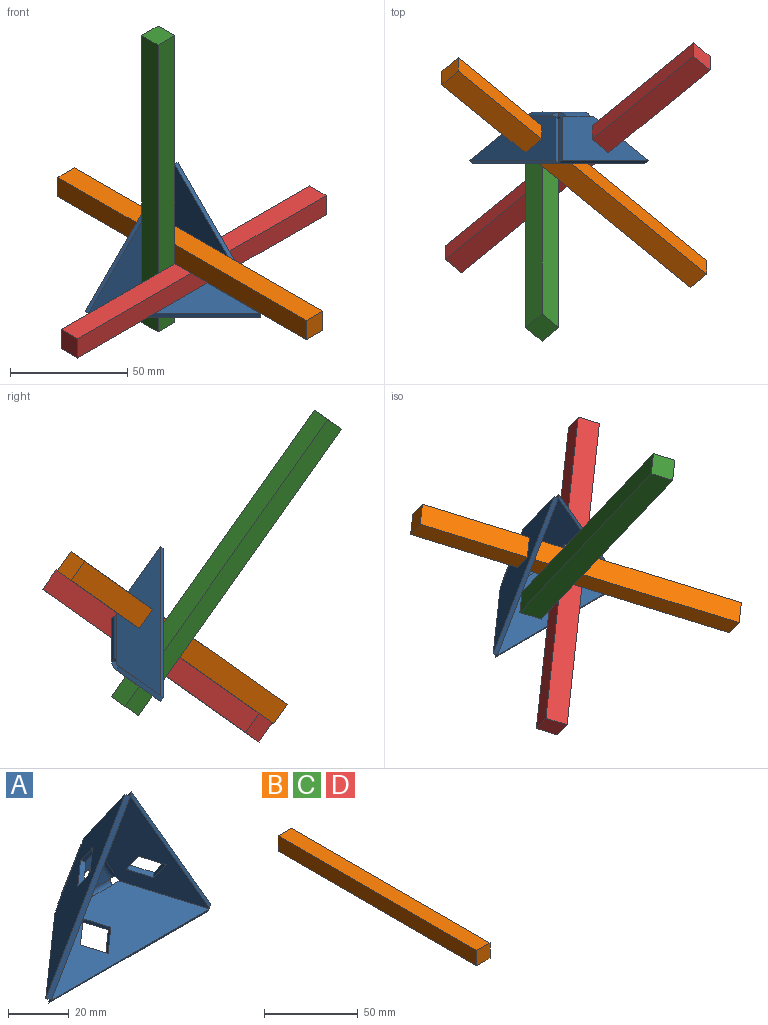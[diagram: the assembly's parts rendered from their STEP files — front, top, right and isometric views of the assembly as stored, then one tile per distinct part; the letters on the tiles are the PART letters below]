
ASSEMBLY  parts=4 mates=6
PART A: 48 faces, bbox 76.5x21.9x66.3 mm
  f0: cylinder r=2.75mm len=5.5mm, axis (0,-1,0), area 34.6mm2, adj f1,f2
  f1: plane 20.9x18.1mm, normal (0,1,0), area 165.4mm2, adj f0,f16,f31,f46
  f2: plane 20.9x18.1mm, normal (0,-1,0), area 165.4mm2, adj f0,f17,f32,f47
  f3: plane 3.59x3.01mm, normal (0.5,0.82,-0.29), area 6.4mm2, adj f5,f12,f13,f14
  f4: plane 64.61x38.24mm, normal (-0.5,-0.82,0.29), area 147.3mm2, adj f5,f11,f12,f13
  f5: plane 27.58x20.08mm, normal (0.71,0.58,0.41), area 65.6mm2, adj f3,f4,f12,f13
  f6: plane 3.59x3.01mm, normal (0.5,0.82,-0.29), area 6.4mm2, adj f11,f12,f13,f15
  f7: plane 8.49x6.93mm, normal (0,0.58,-0.82), area 20mm2, adj f8,f10,f12,f13
  f8: plane 8.98x6.93mm, normal (0.71,0.58,0.41), area 20mm2, adj f7,f9,f12,f13
  f9: plane 8.49x6.93mm, normal (0,-0.58,0.82), area 20mm2, adj f8,f10,f12,f13
  f10: plane 8.98x6.93mm, normal (-0.71,-0.58,-0.41), area 20mm2, adj f7,f9,f12,f13
  f11: plane 24.6x20.08mm, normal (0,0.58,-0.82), area 65.6mm2, adj f4,f6,f12,f13
  f12: plane 63.79x36.83mm, normal (-0.71,0.58,0.41), area 1070.1mm2, adj f3,f4,f5,f6,f7,f8,f9,f10
  f13: plane 63.79x36.83mm, normal (0.71,-0.58,-0.41), area 1070.1mm2, adj f3,f4,f5,f6,f7,f8,f9,f10
  f14: plane 3.03x2.97mm, normal (0.5,0,0.87), area 6.3mm2, adj f3,f16,f17,f30
  f15: plane 3.03x2.97mm, normal (-0.5,0,-0.87), area 6.3mm2, adj f6,f16,f17,f44
  f16: cylinder r=4.29mm len=19.85mm, axis (0.5,0,0.87), area 85.6mm2, adj f1,f12,f14,f15
  f17: cylinder r=2.29mm len=19.03mm, axis (0.5,0,0.87), area 45.6mm2, adj f2,f13,f14,f15
  f18: plane 3.59x3.01mm, normal (-0.5,0.82,-0.29), area 6.4mm2, adj f20,f27,f28,f29
  f19: plane 64.61x38.24mm, normal (0.5,-0.82,0.29), area 147.3mm2, adj f20,f26,f27,f28
  f20: plane 24.6x20.08mm, normal (0,0.58,-0.82), area 65.6mm2, adj f18,f19,f27,f28
  f21: plane 3.59x3.01mm, normal (-0.5,0.82,-0.29), area 6.4mm2, adj f26,f27,f28,f30
  f22: plane 8.98x6.93mm, normal (-0.71,0.58,0.41), area 20mm2, adj f23,f25,f27,f28
  f23: plane 8.49x6.93mm, normal (0,0.58,-0.82), area 20mm2, adj f22,f24,f27,f28
  f24: plane 8.98x6.93mm, normal (0.71,-0.58,-0.41), area 20mm2, adj f23,f25,f27,f28
  f25: plane 8.49x6.93mm, normal (0,-0.58,0.82), area 20mm2, adj f22,f24,f27,f28
  f26: plane 27.58x20.08mm, normal (-0.71,0.58,0.41), area 65.6mm2, adj f19,f21,f27,f28
  f27: plane 63.79x36.83mm, normal (0.71,0.58,0.41), area 1070.1mm2, adj f18,f19,f20,f21,f22,f23,f24,f25
  f28: plane 63.79x36.83mm, normal (-0.71,-0.58,-0.41), area 1070.1mm2, adj f18,f19,f20,f21,f22,f23,f24,f25
  f29: plane 3.03x2.97mm, normal (0.5,0,-0.87), area 6.3mm2, adj f18,f31,f32,f45
  f30: plane 3.03x2.97mm, normal (-0.5,0,0.87), area 6.3mm2, adj f14,f21,f31,f32
  f31: cylinder r=4.29mm len=19.85mm, axis (0.5,0,-0.87), area 85.6mm2, adj f1,f27,f29,f30
  f32: cylinder r=2.29mm len=19.03mm, axis (0.5,0,-0.87), area 45.6mm2, adj f2,f28,f29,f30
  f33: plane 3.2x1.63mm, normal (0,0.82,0.58), area 6.4mm2, adj f35,f42,f43,f44
  f34: plane 73.66x1.63mm, normal (0,-0.82,-0.58), area 147.3mm2, adj f35,f41,f42,f43
  f35: plane 23.18x20.08mm, normal (-0.71,0.58,0.41), area 65.6mm2, adj f33,f34,f42,f43
  f36: plane 3.2x1.63mm, normal (0,0.82,0.58), area 6.4mm2, adj f41,f42,f43,f45
  f37: plane 7.07x6.93mm, normal (0.71,0.58,0.41), area 20mm2, adj f38,f40,f42,f43
  f38: plane 7.07x6.93mm, normal (-0.71,0.58,0.41), area 20mm2, adj f37,f39,f42,f43
  f39: plane 7.07x6.93mm, normal (-0.71,-0.58,-0.41), area 20mm2, adj f38,f40,f42,f43
  f40: plane 7.07x6.93mm, normal (0.71,-0.58,-0.41), area 20mm2, adj f37,f39,f42,f43
  f41: plane 23.18x20.08mm, normal (0.71,0.58,0.41), area 65.6mm2, adj f34,f36,f42,f43
  f42: plane 73.66x18.93mm, normal (0,0.58,-0.82), area 1070.1mm2, adj f33,f34,f35,f36,f37,f38,f39,f40
  f43: plane 73.66x18.93mm, normal (0,-0.58,0.82), area 1070.1mm2, adj f33,f34,f35,f36,f37,f38,f39,f40
  f44: plane 3.5x2.97mm, normal (-1,0,0), area 6.3mm2, adj f15,f33,f46,f47
  f45: plane 3.5x2.97mm, normal (1,0,0), area 6.3mm2, adj f29,f36,f46,f47
  f46: cylinder r=4.29mm len=20.9mm, axis (-1,0,0), area 85.6mm2, adj f1,f42,f44,f45
  f47: cylinder r=2.29mm len=20.9mm, axis (-1,0,0), area 45.6mm2, adj f2,f43,f44,f45
PART B: 6 faces, bbox 10x150x10 mm
  f0: plane 150x10mm, normal (0,0,-1), area 1500mm2, adj f1,f3,f4,f5
  f1: plane 150x10mm, normal (1,0,0), area 1500mm2, adj f0,f2,f4,f5
  f2: plane 150x10mm, normal (0,0,1), area 1500mm2, adj f1,f3,f4,f5
  f3: plane 150x10mm, normal (-1,0,0), area 1500mm2, adj f0,f2,f4,f5
  f4: plane 10x10mm, normal (0,-1,0), area 100mm2, adj f0,f1,f2,f3
  f5: plane 10x10mm, normal (0,1,0), area 100mm2, adj f0,f1,f2,f3
PART C: same geometry as B
PART D: same geometry as B
PLACE A t=(-37.18,3.85,-10.77)mm fixed
PLACE B rot(axis=(0.71,0.46,-0.54),173.1deg) t=(-17.99,-21.98,0.75)mm
PLACE C rot(axis=(-0.74,-0.59,0.31),69.7deg) t=(-31.76,-45.03,32.7)mm
PLACE D rot(axis=(0.59,0.24,-0.77),56.6deg) t=(-16.58,-15.67,-7.03)mm
MATE planar A.f39 <-> C.f1  axis (-0.71,-0.58,-0.41) through (-28.22,-5.45,-17.15)mm
MATE planar A.f9 <-> B.f1  axis (0,-0.58,0.82) through (-34.7,-5.45,6.31)mm
MATE planar D.f1 <-> A.f22  axis (0.71,-0.58,-0.41) through (-13.04,-18.56,-9.08)mm
MATE planar D.f0 <-> A.f25  axis (0,0.58,-0.82) through (-16.58,-12.78,-11.12)mm
MATE planar C.f2 <-> A.f40  axis (-0.71,0.58,0.41) through (-35.29,-42.15,34.74)mm
MATE planar A.f8 <-> B.f2  axis (0.71,0.58,0.41) through (-38.23,-11.23,8.36)mm
